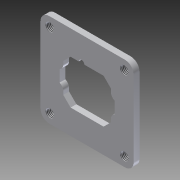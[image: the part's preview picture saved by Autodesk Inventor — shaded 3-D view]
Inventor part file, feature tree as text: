
AUTODESK INVENTOR PART (.ipt)
format: ipt  version: 2012 (Build 160160000, 160)  size: 146,944 bytes
history: native  units: in
note: dims shown in document units (in); Inventor stores cm internally (conversion verified against a paired STEP export)
features: thread x4, fillet x2, sketch x1, extrude x1, hole x1
ambient origin geometry x8: Origin, YZ Plane, XZ Plane, XY Plane, X Axis, Y Axis, Z Axis, Center Point
bodies: Solid1 (feature_tree)
feature tree (9):
  sketch  "Sketch1"  dims[d0=0.9449in d1=0.4724in d2=1.0236in d3=0.5118in d4=0.0787in d5=0.2559in d6=0.128in d7=0.0787in d8=0.5625in d9=2.0in d10=1.0in d11=2.0in d12=1.0in d13=0.1181in d14=0.3937in d15=0.1575in d16=0.1575in d17=0.1575in d18=0.1575in d19=0.1575in d20=0.2in d21=0.2in d22=0.2in d23=0.2in d24=0.125in d25=0.0in d26=0.125in d27=0.18in d28=0.75in d29=0.27in d30=0.2in d31=0.5635in d32=1.0in d33=0.8108in d34=1.6in d35=1.6in d36=1.0in d37=0.0in d38=1.0in d39=0.0in d40=1.0in d41=0.0in d42=1.0in d43=0.0in d44=0.1875in]
  extrude  "Extrusion1"  Depth=0.4724in
  fillet  "Fillet1"  Radius=1.0236in
  hole  "Hole1"  [1 undecoded]
  thread  "Thread1"  [1 undecoded]
  thread  "Thread2"  [1 undecoded]
  thread  "Thread3"  [1 undecoded]
  thread  "Thread4"  [1 undecoded]
  fillet  "Fillet2"  Radius=0.5625in
note: 5 required parameter values undecoded (feature->parameter linkage not recoverable at this tier; creation-order binding heuristic only, values carry confidence <= 0.55)
